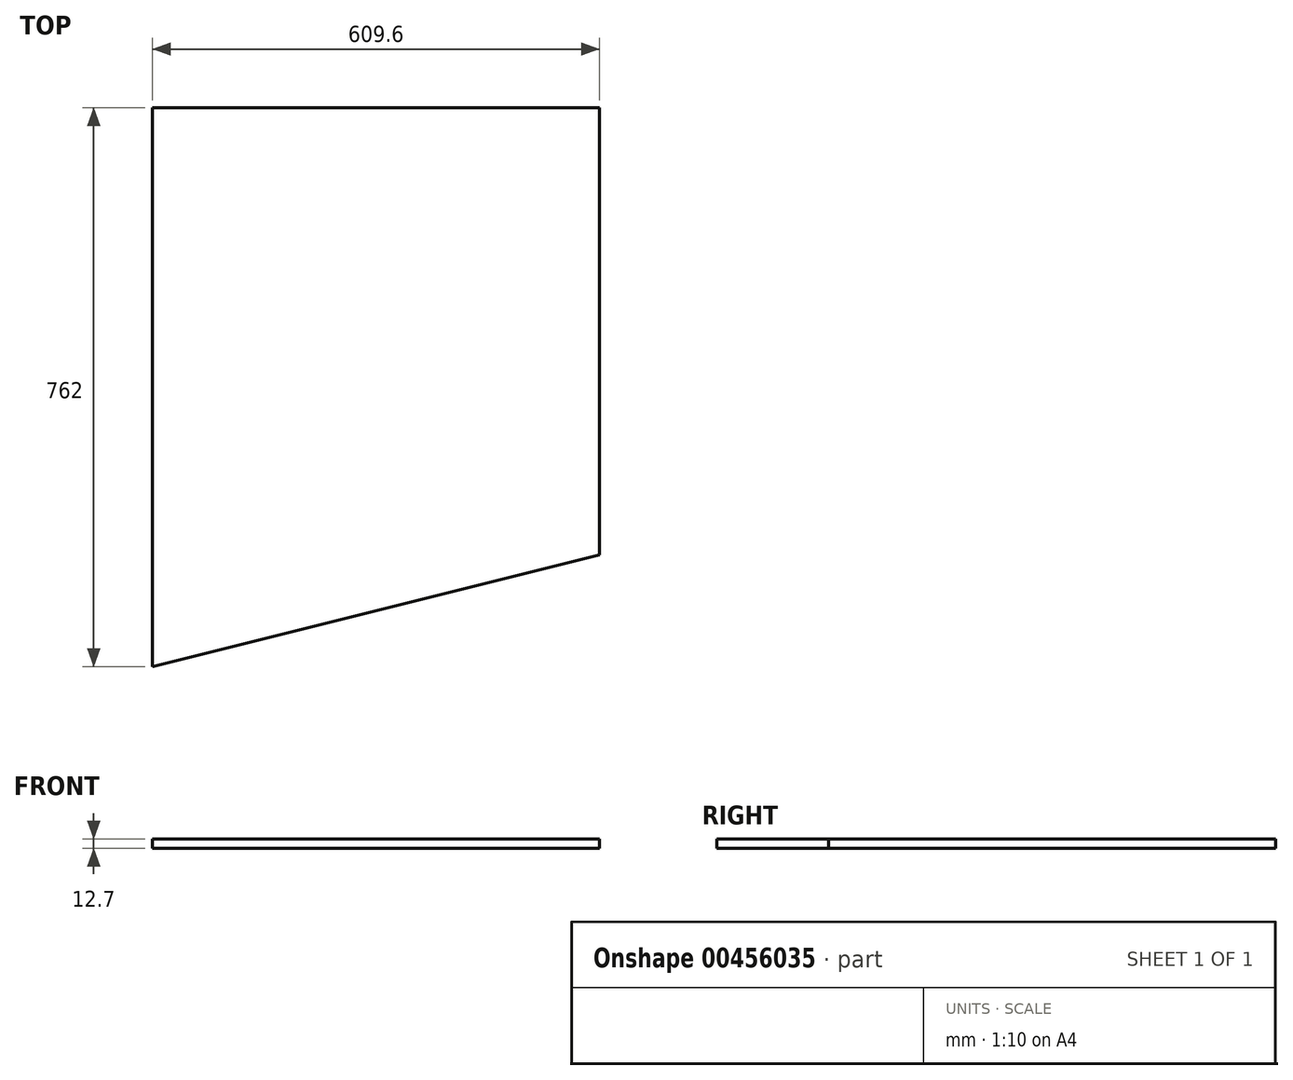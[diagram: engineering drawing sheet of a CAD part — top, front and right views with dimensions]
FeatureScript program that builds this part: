
annotation { "Feature Type Name" : "Feature", "Feature Type Description" : "" }
export const myFeature = defineFeature(function(context is Context, id is Id, definition is map)
    precondition{}
    {
        {
            var Q0;
            Q0=qCreatedBy(makeId("Top.planeOp"),FACE);
            var sketch = newSketch(context, id + "F0", { "sketchPlane" : qUnion([Q0])});
            skLineSegment(sketch, "E0.bottom", {"start": v(0, 0) * mm, "end": v(609.6, 0) * mm});
            skLineSegment(sketch, "E0.left", {"start": v(0, 0) * mm, "end": v(0, -762) * mm});
            skLineSegment(sketch, "E1", {"start": v(609.6, 0) * mm, "end": v(609.6, -609.6) * mm});
            skLineSegment(sketch, "E2", {"start": v(609.6, -609.6) * mm, "end": v(0, -762) * mm});
            skSolve(sketch);
        }
        {
            var Q0;
            Q0=makeQuery(id+"F0.imprint","IMPRINT",FACE,{"disambiguationData":[TD([[makeQuery(id+"F0.imprint","IMPRINT",EDGE,{"derivedFrom":sQuery(id+"F0.wireOp",EDGE,"E0.bottom")}),-1.0]])]});
            extrude(context, id + "F1", {"entities" : qUnion([Q0]), "depth" : 12.7 * mm});
        }
    });
